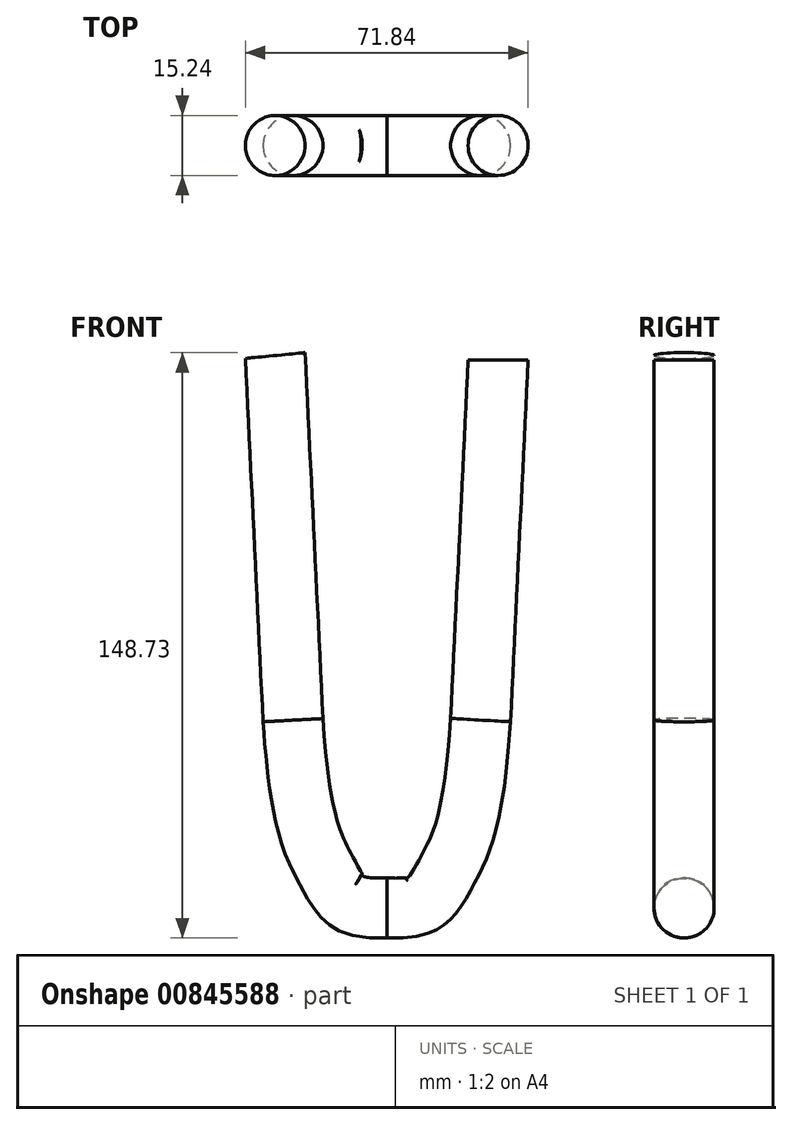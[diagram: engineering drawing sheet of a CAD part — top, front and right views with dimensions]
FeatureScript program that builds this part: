
annotation { "Feature Type Name" : "Feature", "Feature Type Description" : "" }
export const myFeature = defineFeature(function(context is Context, id is Id, definition is map)
    precondition{}
    {
        {
            var Q0;
            Q0=qCreatedBy(makeId("Front.planeOp"),FACE);
            var sketch = newSketch(context, id + "F0", { "sketchPlane" : qUnion([Q0])});
            skPoint(sketch, "E0", {"position": v(40, 0) * mm});
            skLineSegment(sketch, "E1", {"start": v(40, 0) * mm, "end": v(35.51, -92.16) * mm});
            skFitSpline(sketch, "E2", {"points": [v(35.51, -92.16) * mm, v(25.17, -136.23) * mm, v(0, -150.88) * mm], "startDerivative": vector(-10.2, -151.37) * mm, "endDerivative": vector(-112.02, 5.27) * mm});
            skLineSegment(sketch, "E3.MirrorCS", {"start": v(-40, 0) * mm, "end": v(-35.51, -92.16) * mm});
            skFitSpline(sketch, "E4.MirrorCS", {"points": [v(-35.51, -92.16) * mm, v(-25.17, -136.23) * mm, v(0, -150.88) * mm], "startDerivative": vector(10.2, -151.37) * mm, "endDerivative": vector(112.02, 5.27) * mm});
            skSolve(sketch);
        }
        {
            var Q0;
            Q0=qCreatedBy(makeId("Top.planeOp"),FACE);
            var sketch = newSketch(context, id + "F1", { "sketchPlane" : qUnion([Q0])});
            skCircle(sketch, "E5", {"center": v(28.28, 0) * mm, "radius": 7.62 * mm});
            skSolve(sketch);
        }
        {
            var Q0;
            Q0=makeQuery(id+"F1.imprint","IMPRINT",FACE,{"disambiguationData":[TD([[makeQuery(id+"F1.imprint","IMPRINT",EDGE,{"derivedFrom":sQuery(id+"F1.wireOp",EDGE,"E5")}),1.0]])]});
            var Q1;
            Q1=sQuery(id+"F0.wireOp",EDGE,"E1");
            var Q2;
            Q2=sQuery(id+"F0.wireOp",EDGE,"E2");
            var Q3;
            Q3=sQuery(id+"F0.wireOp",EDGE,"E4.MirrorCS");
            var Q4;
            Q4=sQuery(id+"F0.wireOp",EDGE,"E3.MirrorCS");
            sweep(context, id + "F2", {"profiles" : qUnion([Q0]), "path" : qUnion([Q1, Q2, Q3, Q4])});
        }
    });
